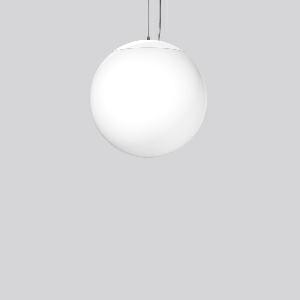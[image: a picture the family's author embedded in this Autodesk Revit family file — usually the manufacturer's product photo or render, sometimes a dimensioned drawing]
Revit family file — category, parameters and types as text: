
# Revit family: basic_ball_312112_002_76_53e9
name_source: partatom
category: Lighting Fixtures
units: mm (PartAtom-declared; Revit-internal decimal feet)

## family parameters
Cut with Voids When Loaded = No
Host = Face
Light Source = No
Part Type = Normal
Room Calculation Point = No
Round Connector Dimension = Use Diameter
Shared = No

## types (1)
- BASIC BALL (1 x LED Modul 930, 9200 lm, 3000)
    Apparent Load = 79 VA
    CIE Flux Codes = 25 50 76 57 100
    Color Rendering = 90
    Color Temperature = 3000
    Default Elevation = 1800 mm
    Description = Series: BASIC BALL
Pendant luminaire in timelessly classic sphere design. Canopy: metal, powder-coated, white. Metal cap: white, powder-coated. Diffuser: shockproof plastic (polyethylene), opal, satin finish. Shadow-free, homogeneous and soft illumination. Single-point steel cable suspension, steplessly adjustable. Special lengths available on request. Power supply cable: white. 
Colour: white
Diameter: 400 mm
Height: 400 mm
Suspension length: 300-4000 mm
Lamp: LED
Socket: without socket
Colour temperature: 3000K
Colour rendering index (CRI): 90
System power: 79 W
Rated luminous flux: 9200 lm
Luminous efficiency: 116 lm/W
Control gear: Converter, dimmable, DALI
Protection class: I
Type of protection: IP 40
    Height = 400 mm
    Lamp = 1 x LED Modul 930
    Lamp Light Flux = 9200 lm
    Lamp count = 1
    Length = 400 mm
    Lifetime = 50000 h
    Luminous efficacy = 116 lm/W
    Manufacturer = RZB
    ModVariant = No
    Model = 312112.002.76
    Mounting Place = Ceiling
    Mounting Type = Pendant
    Number of Poles = 1
    OnlyDefault = Yes
    Power Factor = 1
    Product Name = BASIC BALL
    Product group = Pendant luminaires
    ProductGroupID = 902
    Protection Class = Protection class I
    Protection Degree = IP 40
    RLX_Detail_Level = 1
    RLX_Emergency_Light_Flux = 0 lm
    RLX_Emergency_Type = 0
    RLX_Emergency_Type_DB = No
    RlxData = <blob elided: 53457 chars, md5=cdb8450a>
    Socket = socket
    Standby Power = 0 W
    System Light Flux = 9200 lm
    System Power = 79 W
    Type Comments = Product without accessories
    Type Image = 312105.002.jpg
    URL = http://relux.com
    VarID = ---
    Voltage = 230 V
    Voltage Range = 220-240 V
    Weight = 0.00 kg
    Width = 0 mm  [stored 0 ft]

note: [stored X ft] marks values corroborated as IEEE doubles in the binary element streams (Revit-internal decimal feet)

## geometry (parser evidence)
native form markers: Blend x4, Sweep x13
no freeform markers — native parametric forms only
